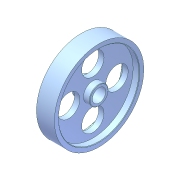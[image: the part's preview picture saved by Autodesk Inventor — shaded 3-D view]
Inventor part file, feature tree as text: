
AUTODESK INVENTOR PART (.ipt)
format: ipt  version: unknown  size: 222,720 bytes
history: native  units: in
note: dims shown in document units (in); Inventor stores cm internally (conversion verified against a paired STEP export)
features: sketch x2, revolve x1, chamfer x1, extrude x1, pattern_circular x1
ambient origin geometry x8: Origin, YZ Plane, XZ Plane, XY Plane, X Axis, Y Axis, Z Axis, Center Point
feature tree (6):
  revolve  "Revolution1"  [1 undecoded]
  chamfer  "Chamfer1"  Distance=0.1181in
  extrude  "Extrusion3"  Depth=0.0197in TaperAngle=45.0deg
  pattern_circular  "Circular Pattern3"  [2 undecoded]
  sketch  "Sketch1"  dims[d0=1.9685in d2=0.2756in d4=0.2953in]
  sketch  "Sketch4"  dims[d5=90.0deg d14=0.1181in d19=0.0197in d20=0.0787in d21=45.0deg d24=0.1969in d25=0.1181in d30=0.3937in d31=0.7874in d35=0.3937in d36=0.9843in d37=1.063in d38=0.3937in d39=0.0in d40=1.5748in d41=360.0deg]
note: 3 required parameter values undecoded (feature->parameter linkage not recoverable at this tier; creation-order binding heuristic only, values carry confidence <= 0.55)